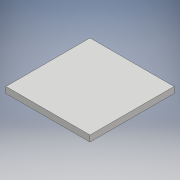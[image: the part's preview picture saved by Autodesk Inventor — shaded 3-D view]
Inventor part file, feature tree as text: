
AUTODESK INVENTOR PART (.ipt)
format: ipt  version: 2018.3 (Build 223284000, 284)  size: 91,648 bytes
history: native  units: mm
features: extrude x1, sketch x1
ambient origin geometry x8: Origin, YZ Plane, XZ Plane, XY Plane, X Axis, Y Axis, Z Axis, Center Point
bodies: Solid1 (feature_tree)
feature tree (2):
  extrude  "Extrusion1"  Depth=13.7mm
  sketch  "Sketch1"  dims[d0=13.7mm d1=13.7mm d2=1.0mm d3=0.0mm]
